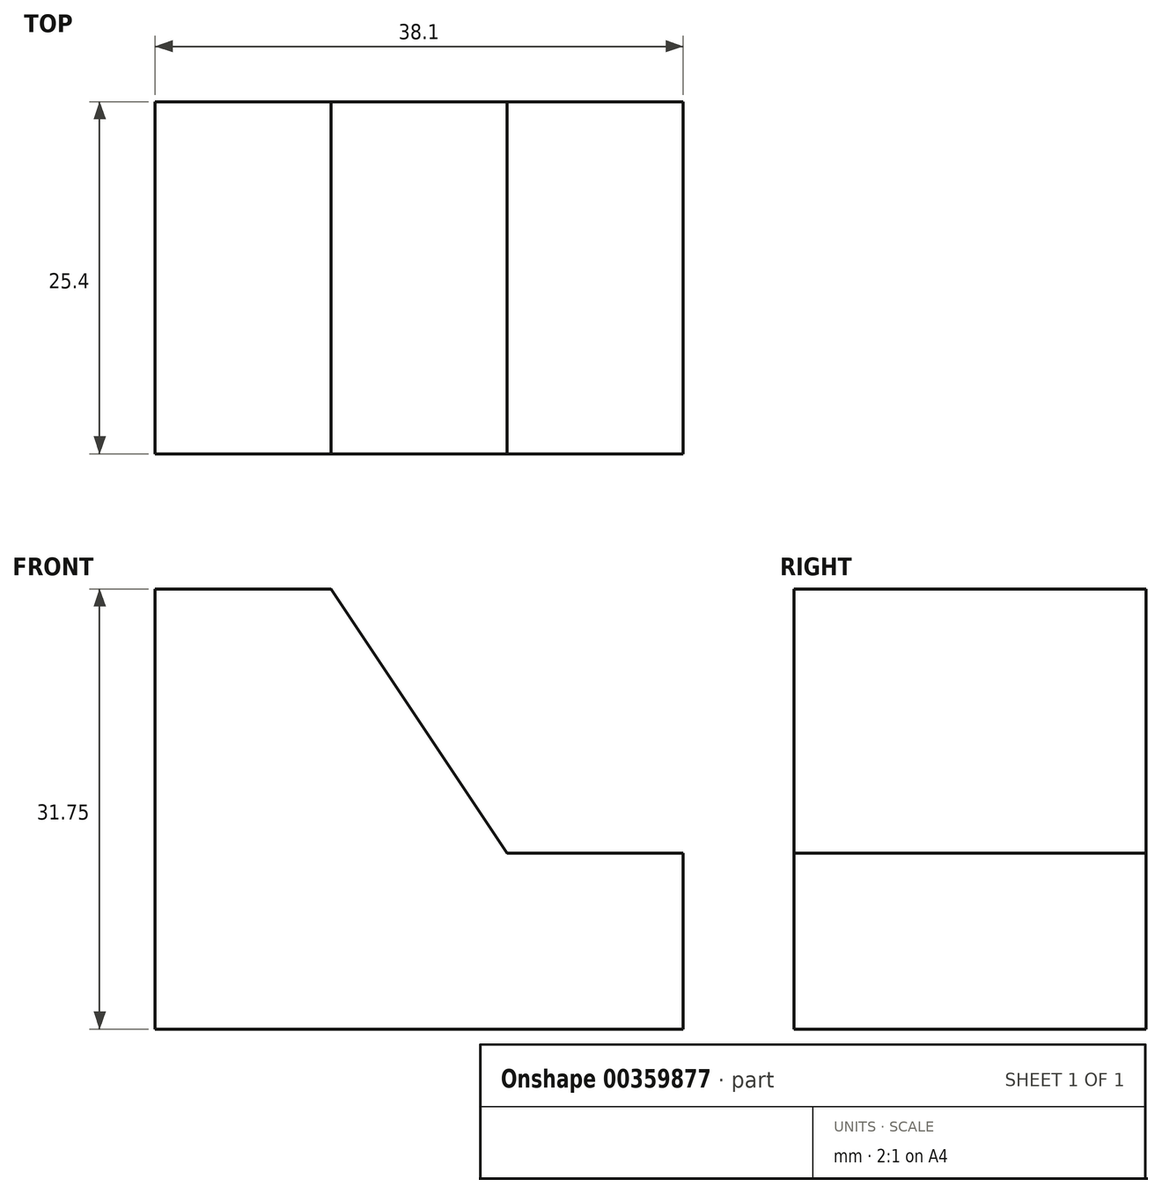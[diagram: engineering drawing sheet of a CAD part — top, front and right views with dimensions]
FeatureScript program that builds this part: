
annotation { "Feature Type Name" : "Feature", "Feature Type Description" : "" }
export const myFeature = defineFeature(function(context is Context, id is Id, definition is map)
    precondition{}
    {
        {
            var Q0;
            Q0=qCreatedBy(makeId("Front.planeOp"),FACE);
            var sketch = newSketch(context, id + "F0", { "sketchPlane" : qUnion([Q0])});
            skLineSegment(sketch, "E0", {"start": v(0, 0) * mm, "end": v(38.1, 0) * mm});
            skLineSegment(sketch, "E1", {"start": v(38.1, 0) * mm, "end": v(38.1, 31.75) * mm});
            skLineSegment(sketch, "E2", {"start": v(38.1, 31.75) * mm, "end": v(0, 31.75) * mm});
            skLineSegment(sketch, "E3", {"start": v(0, 31.75) * mm, "end": v(0, 0) * mm});
            skSolve(sketch);
        }
        {
            var Q0;
            Q0=makeQuery(id+"F0.imprint","IMPRINT",FACE,{"disambiguationData":[TD([[makeQuery(id+"F0.imprint","IMPRINT",EDGE,{"derivedFrom":sQuery(id+"F0.wireOp",EDGE,"E0")}),1.0]])]});
            extrude(context, id + "F1", {"entities" : qUnion([Q0]), "depth" : 25.4 * mm});
        }
        {
            var Q0;
            Q0=makeQuery(id+"F1.opExtrude","CAP_FACE",FACE,{"disambiguationData":[OSD([sQuery(id+"F0.wireOp",EDGE,"E0"),sQuery(id+"F0.wireOp",EDGE,"E1"),sQuery(id+"F0.wireOp",EDGE,"E2"),sQuery(id+"F0.wireOp",EDGE,"E3")])],"isStart":false});
            var sketch = newSketch(context, id + "F2", { "sketchPlane" : qUnion([Q0])});
            skLineSegment(sketch, "E4", {"start": v(38.1, 12.7) * mm, "end": v(25.4, 12.7) * mm});
            skLineSegment(sketch, "E5", {"start": v(25.4, 12.7) * mm, "end": v(25.4, 31.75) * mm});
            skSolve(sketch);
        }
        {
            var Q0;
            {var subQ0=sQuery(id+"F2.wireOp",EDGE,"E4");Q0=makeQuery(id+"F2.imprint","IMPRINT",FACE,{"disambiguationData":[TD([[makeQuery(id+"F2.imprint","IMPRINT",EDGE,{"derivedFrom":subQ0}),-1.0]])]});}
            extrude(context, id + "F3", {"entities" : qUnion([Q0]), "operationType" : NewBodyOperationType.REMOVE, "oppositeDirection" : true, "depth" : 25.4 * mm});
        }
        {
            var Q0;
            Q0=makeQuery(id+"F1.opExtrude","CAP_FACE",FACE,{"disambiguationData":[OSD([sQuery(id+"F0.wireOp",EDGE,"E0"),sQuery(id+"F0.wireOp",EDGE,"E1"),sQuery(id+"F0.wireOp",EDGE,"E2"),sQuery(id+"F0.wireOp",EDGE,"E3")])],"isStart":false});
            var sketch = newSketch(context, id + "F4", { "sketchPlane" : qUnion([Q0])});
            skLineSegment(sketch, "E6", {"start": v(25.4, 12.7) * mm, "end": v(12.7, 31.75) * mm});
            skSolve(sketch);
        }
        {
            var Q0;
            {var subQ0=sQuery(id+"F4.wireOp",EDGE,"E6");Q0=makeQuery(id+"F4.imprint","IMPRINT",FACE,{"disambiguationData":[TD([[makeQuery(id+"F4.imprint","IMPRINT",EDGE,{"derivedFrom":subQ0}),-1.0]])]});}
            extrude(context, id + "F5", {"entities" : qUnion([Q0]), "operationType" : NewBodyOperationType.REMOVE, "oppositeDirection" : true, "depth" : 25.4 * mm});
        }
    });
